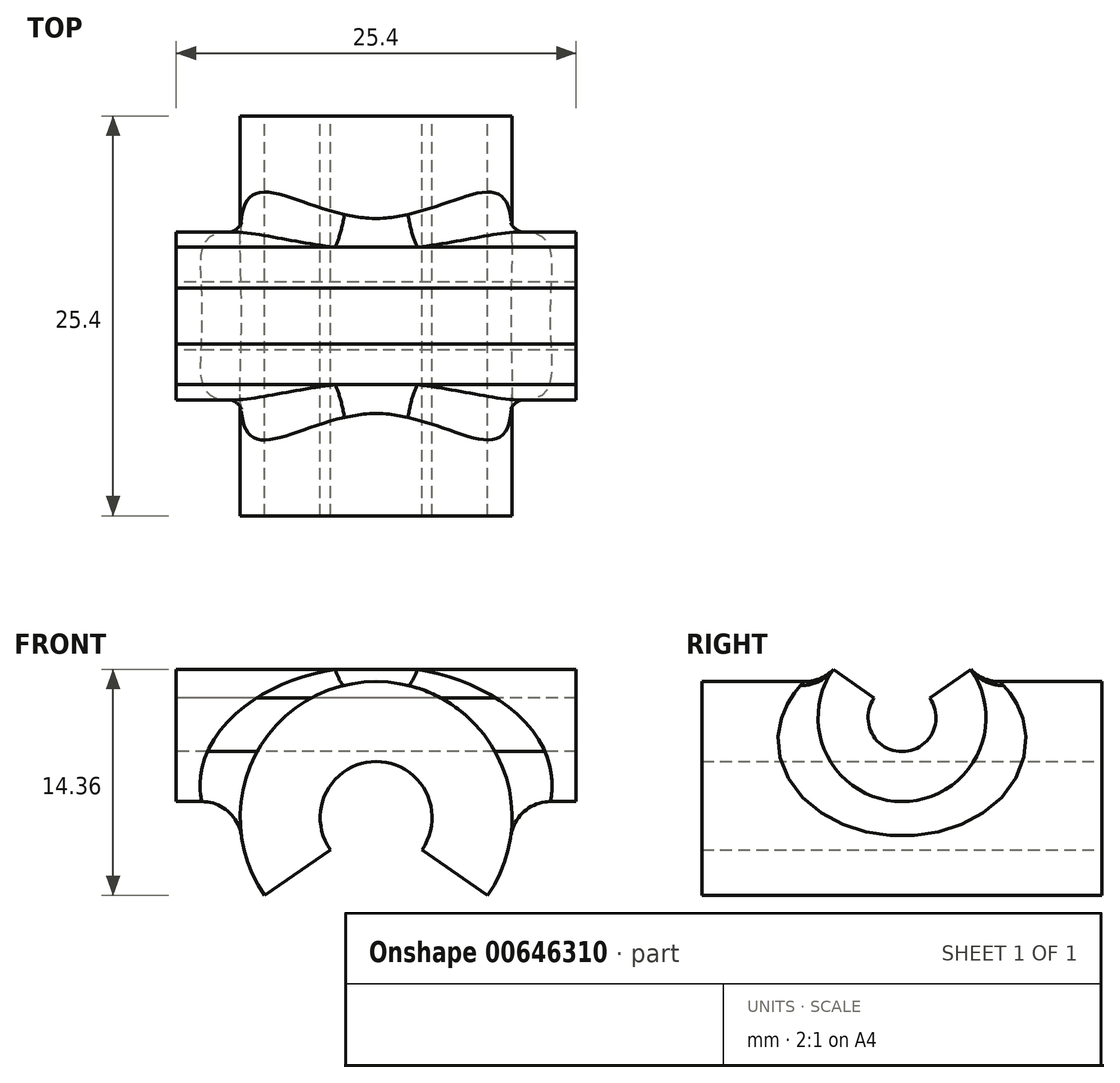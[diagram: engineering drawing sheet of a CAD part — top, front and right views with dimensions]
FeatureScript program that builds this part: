
annotation { "Feature Type Name" : "Feature", "Feature Type Description" : "" }
export const myFeature = defineFeature(function(context is Context, id is Id, definition is map)
    precondition{}
    {
        {
            var Q0;
            Q0=qCreatedBy(makeId("Front.planeOp"),FACE);
            var sketch = newSketch(context, id + "F0", { "sketchPlane" : qUnion([Q0])});
            skLineSegment(sketch, "E0", {"start": v(0, 0) * mm, "end": v(2.91, -2.04) * mm, "construction": true});
            skLineSegment(sketch, "E1", {"start": v(0, 0) * mm, "end": v(0, -3.65) * mm, "construction": true});
            skArc(sketch, "E2.0", {"start": v(2.91, -2.04) * mm, "mid": v(0, 3.56) * mm, "end": v(-2.91, -2.04) * mm});
            skLineSegment(sketch, "E3.MirrorCS", {"start": v(0, 0) * mm, "end": v(-2.91, -2.04) * mm, "construction": true});
            skArc(sketch, "E4.0", {"start": v(7.07, -4.95) * mm, "mid": v(0, 8.64) * mm, "end": v(-7.07, -4.95) * mm});
            skLineSegment(sketch, "E5", {"start": v(-2.91, -2.04) * mm, "end": v(-7.07, -4.95) * mm});
            skLineSegment(sketch, "E6", {"start": v(2.91, -2.04) * mm, "end": v(7.07, -4.95) * mm});
            skSolve(sketch);
        }
        {
            var Q0;
            Q0 = qSketchRegion(id + "F0", true);
            extrude(context, id + "F1", {"entities" : qUnion([Q0]), "endBound" : BoundingType.SYMMETRIC, "depth" : 25.4 * mm, "offsetDistance" : 25.4 * mm});
        }
        {
            var Q0;
            Q0=qCreatedBy(makeId("Right.planeOp"),FACE);
            var sketch = newSketch(context, id + "F2", { "sketchPlane" : qUnion([Q0])});
            skArc(sketch, "E7", {"start": v(-1.77, 7.59) * mm, "mid": v(0, 4.2) * mm, "end": v(1.77, 7.59) * mm});
            skLineSegment(sketch, "E8", {"start": v(0, 6.35) * mm, "end": v(0, 14.8) * mm, "construction": true});
            skLineSegment(sketch, "E9", {"start": v(0, 6.35) * mm, "end": v(1.77, 7.59) * mm, "construction": true});
            skLineSegment(sketch, "E10.MirrorCS", {"start": v(0, 6.35) * mm, "end": v(-1.77, 7.59) * mm, "construction": true});
            skArc(sketch, "E11.0", {"start": v(-4.37, 9.4) * mm, "mid": v(0, 1.02) * mm, "end": v(4.37, 9.4) * mm});
            skLineSegment(sketch, "E12", {"start": v(-1.77, 7.59) * mm, "end": v(-4.37, 9.4) * mm});
            skLineSegment(sketch, "E13", {"start": v(1.77, 7.59) * mm, "end": v(4.37, 9.4) * mm});
            skSolve(sketch);
        }
        {
            var Q0;
            Q0 = qSketchRegion(id + "F2", true);
            extrude(context, id + "F3", {"entities" : qUnion([Q0]), "operationType" : NewBodyOperationType.ADD, "endBound" : BoundingType.SYMMETRIC, "depth" : 25.4 * mm, "offsetDistance" : 25.4 * mm});
        }
        {
            var Q0;
            Q0=qCreatedBy(makeId("Right.planeOp"),FACE);
            var sketch = newSketch(context, id + "F4", { "sketchPlane" : qUnion([Q0])});
            skArc(sketch, "E14.0", {"start": v(-1.77, 7.59) * mm, "mid": v(0, 4.2) * mm, "end": v(1.77, 7.59) * mm});
            skLineSegment(sketch, "E15.0", {"start": v(-1.77, 7.59) * mm, "end": v(-4.37, 9.4) * mm});
            skLineSegment(sketch, "E16.0", {"start": v(1.77, 7.59) * mm, "end": v(4.37, 9.4) * mm});
            skLineSegment(sketch, "E17", {"start": v(-4.37, 9.4) * mm, "end": v(4.37, 9.4) * mm});
            skSolve(sketch);
        }
        {
            var Q0;
            Q0 = qSketchRegion(id + "F4", true);
            extrude(context, id + "F5", {"entities" : qUnion([Q0]), "operationType" : NewBodyOperationType.REMOVE, "endBound" : BoundingType.THROUGH_ALL, "oppositeDirection" : true, "depth" : 25.4 * mm, "offsetDistance" : 25.4 * mm, "hasSecondDirection" : true, "secondDirectionBound" : SecondDirectionBoundingType.THROUGH_ALL, "secondDirectionOppositeDirection" : false, "secondDirectionDepth" : 25.4 * mm});
        }
        {
            var Q0;
            Q0=qCreatedBy(makeId("Front.planeOp"),FACE);
            var sketch = newSketch(context, id + "F6", { "sketchPlane" : qUnion([Q0])});
            skArc(sketch, "E18.0", {"start": v(2.91, -2.04) * mm, "mid": v(0, 3.56) * mm, "end": v(-2.91, -2.04) * mm});
            skLineSegment(sketch, "E19", {"start": v(-2.91, -2.04) * mm, "end": v(2.91, -2.04) * mm});
            skSolve(sketch);
        }
        {
            var Q0;
            Q0 = qSketchRegion(id + "F6", true);
            extrude(context, id + "F7", {"entities" : qUnion([Q0]), "operationType" : NewBodyOperationType.REMOVE, "endBound" : BoundingType.THROUGH_ALL, "oppositeDirection" : true, "depth" : 25.4 * mm, "offsetDistance" : 25.4 * mm, "hasSecondDirection" : true, "secondDirectionBound" : SecondDirectionBoundingType.THROUGH_ALL, "secondDirectionOppositeDirection" : false, "secondDirectionDepth" : 25.4 * mm});
        }
        {
            var Q0;
            Q0=makeQuery(id+"F3.boolean.opBoolean","INTERSECT",EDGE,{"derivedFrom":[makeQuery(id+"F1.opExtrude","SWEPT_FACE",FACE,{"disambiguationData":[OSD([sQuery(id+"F0.wireOp",EDGE,"E4.0")])]}),makeQuery(id+"F3.opExtrude","SWEPT_FACE",FACE,{"disambiguationData":[OSD([sQuery(id+"F2.wireOp",EDGE,"E11.0")])]})]});
            fillet(context, id + "F8", {"entities" : qUnion([Q0]), "radius" : 2.54 * mm, "tangentPropagation" : true, "allowEdgeOverflow" : false});
        }
    });
